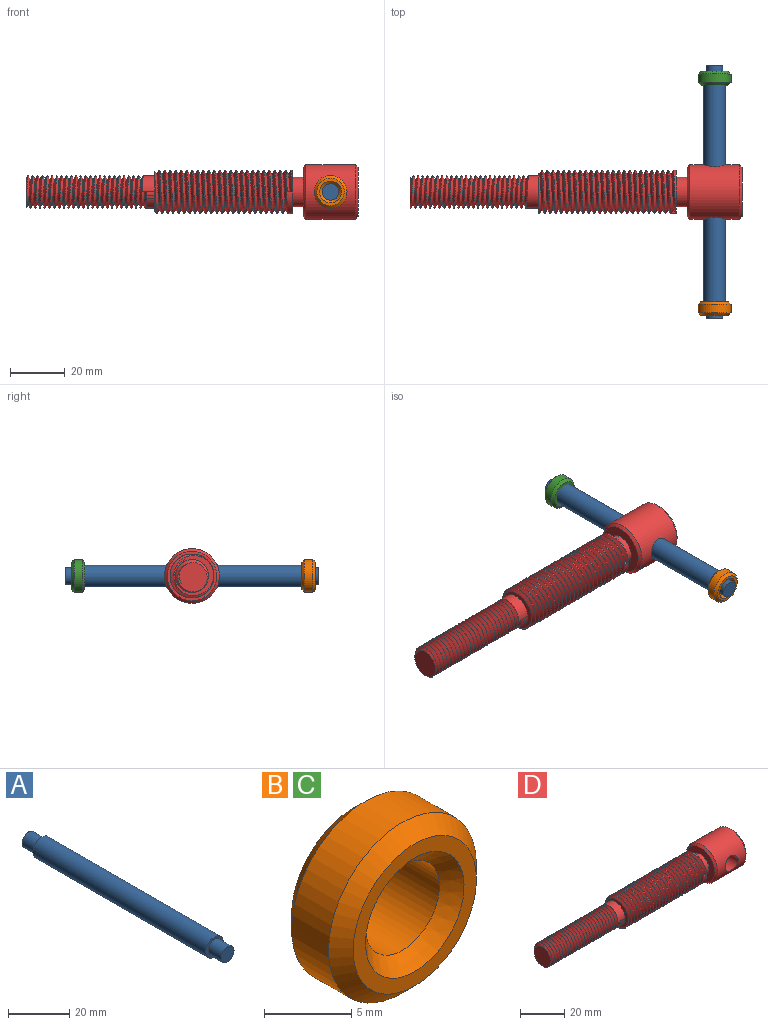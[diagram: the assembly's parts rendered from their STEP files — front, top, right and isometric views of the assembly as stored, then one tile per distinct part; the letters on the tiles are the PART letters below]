
ASSEMBLY  parts=4 mates=3
PART A: 7 faces, bbox 8x92x8 mm
  f0: cylinder r=4mm len=80mm, axis (0,1,0), area 2010.6mm2, adj f1,f4
  f1: plane 8x8mm, normal (0,-1,0), area 22mm2, adj f0,f2
  f2: cylinder r=3mm len=6mm, axis (0,1,0), area 113.1mm2, adj f1,f3
  f3: plane 6x6mm, normal (0,-1,0), area 28.3mm2, adj f2
  f4: plane 8x8mm, normal (0,1,0), area 22mm2, adj f0,f5
  f5: cylinder r=3mm len=6mm, axis (0,-1,0), area 113.1mm2, adj f4,f6
  f6: plane 6x6mm, normal (0,1,0), area 28.3mm2, adj f5
PART B: 7 faces, bbox 12x5x12 mm
  f0: cylinder r=6mm len=12mm, axis (0,1,0), area 113.1mm2, adj f5,f6
  f1: plane 10x10mm, normal (0,-1,0), area 28.3mm2, adj f4,f5
  f2: plane 10x10mm, normal (0,1,0), area 50.3mm2, adj f3,f6
  f3: cylinder r=3mm len=6mm, axis (0,-1,0), area 75.4mm2, adj f2,f4
  f4: cone r=3mm half-angle=45deg, axis (0,-1,0), area 31.1mm2, adj f1,f3
  f5: cone r=5mm half-angle=45deg, axis (0,1,0), area 48.9mm2, adj f0,f1
  f6: cone r=6mm half-angle=45deg, axis (0,-1,0), area 48.9mm2, adj f0,f2
PART C: same geometry as B
PART D: 23 faces, bbox 123.1x21.2x21.2 mm
  f0: cylinder r=8mm len=50mm, axis (-1,0,0), area 372.6mm2, adj f12,f13,f20,f21,f22
  f1: cylinder r=10mm len=20mm, axis (-1,0,0), area 1023mm2, adj f17,f18,f19
  f2: plane 10.67x10.66mm, normal (-1,0,0), area 89.1mm2, adj f3,f4,f5,f6
  f3: plane 0.12x0.1mm, normal (0,-0.78,0.62), area 0mm2, adj f2,f4,f6
  f4: bspline ~5.93x2.22mm, area 0.1mm2, adj f2,f3,f5
  f5: bspline ~44.05x11.85mm, area 1229.7mm2, adj f2,f4,f6,f7
  f6: bspline ~44.92x13.68mm, area 1256.9mm2, adj f2,f3,f5,f7,f8,f10
  f7: plane 4.7x1.3mm, normal (0,0,-1), area 1.7mm2, adj f5,f6,f8,f9,f10,f12
  f8: bspline ~13.86x12mm, area 3.3mm2, adj f6,f7,f9,f11
  f9: cylinder r=6mm len=12mm, axis (-1,0,0), area 135mm2, adj f7,f8,f11,f12
  f10: extruded ~3x1.2mm, area 3.6mm2, adj f6,f7,f11,f12
  f11: extruded ~3x1.11mm, area 3.4mm2, adj f8,f9,f10,f12
  f12: plane 15.86x15.83mm, normal (-1,0,0), area 55.2mm2, adj f0,f7,f9,f10,f11,f20,f21
  f13: plane 16x16mm, normal (1,0,0), area 109.5mm2, adj f0,f14
  f14: cylinder r=5.4mm len=10.8mm, axis (-1,0,0), area 135.7mm2, adj f13,f16
  f15: plane 18x18mm, normal (1,0,0), area 254.5mm2, adj f17
  f16: plane 18x18mm, normal (-1,0,0), area 162.9mm2, adj f14,f18
  f17: cone r=9mm half-angle=45deg, axis (-1,0,0), area 84.4mm2, adj f1,f15
  f18: cone r=10mm half-angle=45deg, axis (1,0,0), area 84.4mm2, adj f1,f16
  f19: cylinder r=4.1mm len=18.24mm, axis (0,1,0), area 469.9mm2, adj f1
  f20: bspline ~50.9x18.48mm, area 2019.9mm2, adj f0,f12,f21,f22
  f21: bspline ~50.23x18.48mm, area 1984.6mm2, adj f0,f12,f20,f22
  f22: plane 1.8x1.56mm, normal (0,0,1), area 1.4mm2, adj f0,f20,f21
PLACE A t=(95.73,29.05,-8.51)mm
PLACE B t=(95.73,-10.95,-8.51)mm
PLACE C rot(axis=(1,0,0),180deg) t=(95.73,68.05,-8.51)mm
PLACE D t=(-18.27,29.05,-8.51)mm
MATE fastened B.f3 <-> A.f2  axis (0,-1,0) through (95.73,-10.95,-8.51)mm
MATE fastened C.f0 <-> A.f0  axis (0,1,0) through (95.73,69.05,-8.51)mm
MATE fastened A.f0 <-> D.f19  axis (0,1,0) through (95.73,29.05,-8.51)mm
